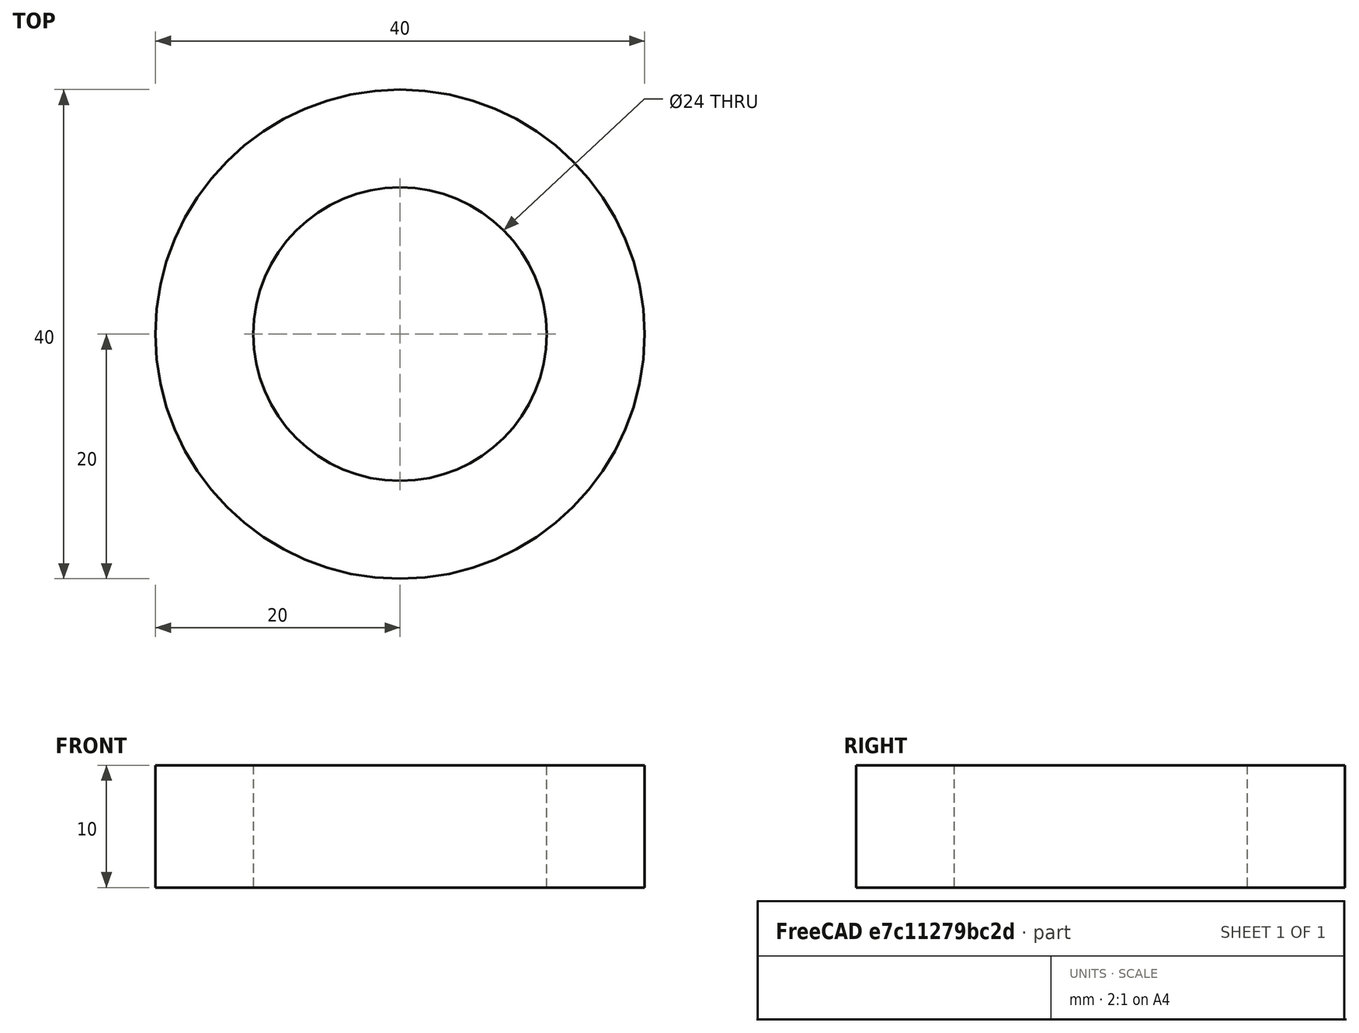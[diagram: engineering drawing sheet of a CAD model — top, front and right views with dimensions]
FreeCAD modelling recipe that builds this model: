
FCSTD DOCUMENT  (FreeCAD 0.19R24276 (Git))
Label: ring_24x40
License: All rights reserved
LicenseURL: http://en.wikipedia.org/wiki/All_rights_reserved
objects: Sketcher::SketchObject×1, PartDesign::Pad×1, PartDesign::Body×1
note: 4 computed .brp shape members not serialized (recipe doc carries the construction recipe); baked Part::Feature solids carry a one-line shape summary decoded from their .brp

FEATURE [Sketcher::SketchObject] Sketch
  FullyConstrained = true
  MapMode = 5
  Support = -> [XY_Plane]
  sketch-geometry (2):
    g0: Circle CenterX=0 CenterY=0 CenterZ=0 NormalX=0 NormalY=0 NormalZ=1 AngleXU=0 Radius=12
    g1: Circle CenterX=0 CenterY=0 CenterZ=0 NormalX=0 NormalY=0 NormalZ=1 AngleXU=0 Radius=20
  constraints (4):
    c: Coincident(g0,g-1)
    c: Coincident(g1,g0)
    c: Diameter(g0) = 24
    c: Diameter(g1) = 40
FEATURE [PartDesign::Pad] Pad
  Direction = (1,1,1)
  Length = 10
  Length2 = 100
  Profile = -> Sketch
  Type = 0
FEATURE [PartDesign::Body] Body
  Group = -> [Sketch,Pad]
  Origin = -> Origin
  Tip = -> Pad
